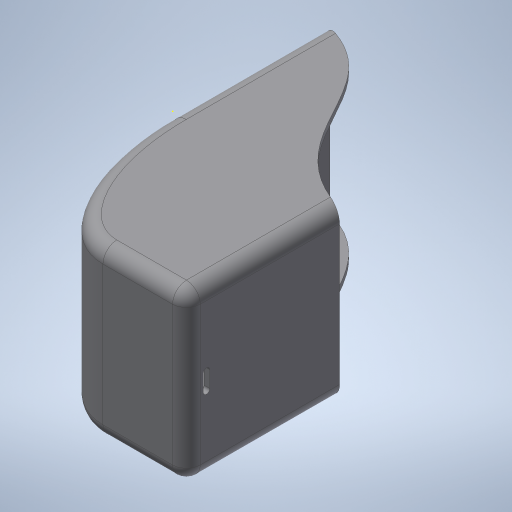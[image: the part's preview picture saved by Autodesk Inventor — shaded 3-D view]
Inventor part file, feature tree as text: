
AUTODESK INVENTOR PART (.ipt)
format: ipt  version: 2023.1 (Build 271208000, 208)  size: 353,792 bytes
history: native  units: mm
features: sketch x4, extrude x3, shell x1, fillet x1, projected_geometry x1
ambient origin geometry x8: Origin, YZ Plane, XZ Plane, XY Plane, X Axis, Y Axis, Z Axis, Center Point
bodies: Solid1 (feature_tree)
feature tree (10):
  extrude  "Extrusion1"  Depth=60.0mm
  sketch  "Sketch3"  dims[d4=150.0mm d5=60.0mm d6=0.0mm d12=60.0mm d13=0.0mm]
  extrude  "Extrusion3"  Depth=60.0mm TaperAngle=0.0deg
  shell  "Shell2"  Thickness=60.0mm
  extrude  "Extrusion4"  Depth=6.0mm
  fillet  "Fillet2"  Radius=1.2mm
  sketch  "Sketch1"  dims[d0=60.0mm d1=95.0mm d2=40.0mm d3=60.0mm]
  sketch  "Sketch4"  dims[d14=2.0mm d15=6.0mm d16=1.2mm]
  projected_geometry  "Projected Loop2"
  sketch  "Sketch5"  dims[d17=2.4mm d18=8.25mm d19=1.2mm d20=1.2mm d21=5.0mm d22=0.0mm d23=5.0mm d8=0.5mm d9=0.872665mm d10=0.5mm d11=0.872665mm]
